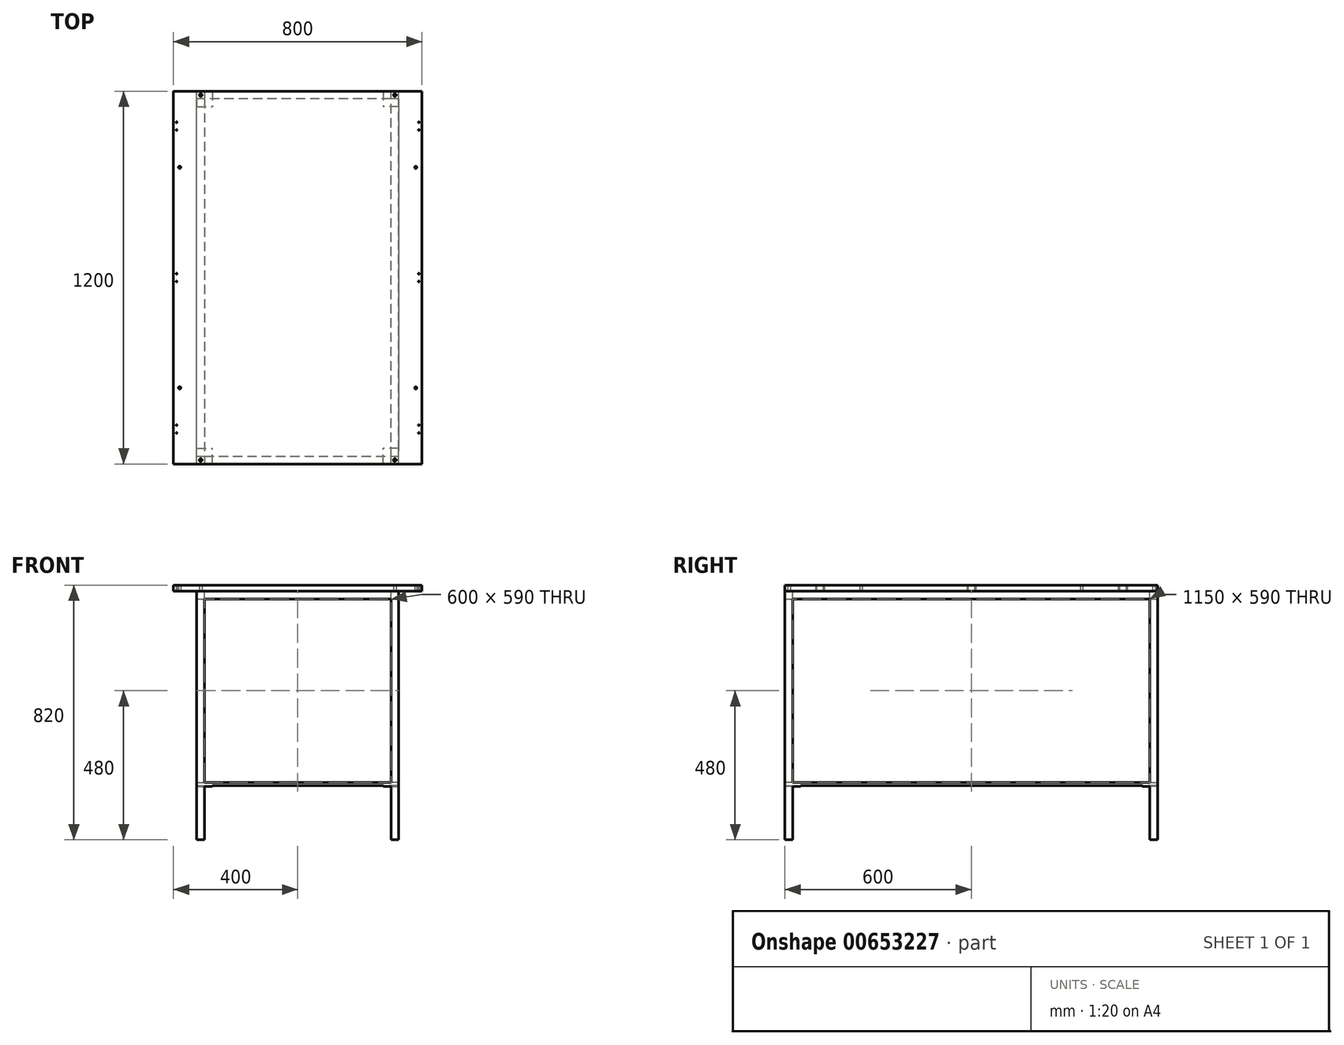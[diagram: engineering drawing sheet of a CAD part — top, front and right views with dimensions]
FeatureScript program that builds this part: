
annotation { "Feature Type Name" : "Feature", "Feature Type Description" : "" }
export const myFeature = defineFeature(function(context is Context, id is Id, definition is map)
    precondition{}
    {
        {
            var Q0;
            Q0=qCreatedBy(makeId("Top.planeOp"),FACE);
            var sketch = newSketch(context, id + "F0", { "sketchPlane" : qUnion([Q0])});
            skLineSegment(sketch, "E0.bottom", {"start": v(400, 600) * mm, "end": v(-400, 600) * mm});
            skLineSegment(sketch, "E0.top", {"start": v(400, -600) * mm, "end": v(-400, -600) * mm});
            skLineSegment(sketch, "E0.left", {"start": v(400, 600) * mm, "end": v(400, -600) * mm});
            skLineSegment(sketch, "E0.right", {"start": v(-400, 600) * mm, "end": v(-400, -600) * mm});
            skPoint(sketch, "E0.middle", {"position": v(0, 0) * mm});
            skSolve(sketch);
        }
        {
            var Q0;
            Q0=makeQuery(id+"F0.imprint","IMPRINT",FACE,{"disambiguationData":[TD([[makeQuery(id+"F0.imprint","IMPRINT",EDGE,{"derivedFrom":sQuery(id+"F0.wireOp",EDGE,"E0.bottom")}),1.0]])]});
            extrude(context, id + "F1", {"entities" : qUnion([Q0]), "depth" : 20 * mm, "offsetDistance" : 25 * mm});
        }
        {
            var Q0;
            Q0=makeQuery(id+"F1.opExtrude","CAP_FACE",FACE,{"disambiguationData":[OSD([sQuery(id+"F0.wireOp",EDGE,"E0.bottom"),sQuery(id+"F0.wireOp",EDGE,"E0.top"),sQuery(id+"F0.wireOp",EDGE,"E0.left"),sQuery(id+"F0.wireOp",EDGE,"E0.right")])],"isStart":true});
            var sketch = newSketch(context, id + "F2", { "sketchPlane" : qUnion([Q0])});
            skLineSegment(sketch, "E1.bottom", {"start": v(-325, 600) * mm, "end": v(-300, 600) * mm});
            skLineSegment(sketch, "E1.top", {"start": v(-325, 575) * mm, "end": v(-300, 575) * mm});
            skLineSegment(sketch, "E1.left", {"start": v(-325, 600) * mm, "end": v(-325, 575) * mm});
            skLineSegment(sketch, "E1.right", {"start": v(-300, 600) * mm, "end": v(-300, 575) * mm});
            skLineSegment(sketch, "E2.bottom", {"start": v(300, 600) * mm, "end": v(325, 600) * mm});
            skLineSegment(sketch, "E2.top", {"start": v(300, 575) * mm, "end": v(325, 575) * mm});
            skLineSegment(sketch, "E2.left", {"start": v(300, 600) * mm, "end": v(300, 575) * mm});
            skLineSegment(sketch, "E2.right", {"start": v(325, 600) * mm, "end": v(325, 575) * mm});
            skLineSegment(sketch, "E3.bottom", {"start": v(-300, -575) * mm, "end": v(-325, -575) * mm});
            skLineSegment(sketch, "E3.top", {"start": v(-300, -600) * mm, "end": v(-325, -600) * mm});
            skLineSegment(sketch, "E3.left", {"start": v(-300, -575) * mm, "end": v(-300, -600) * mm});
            skLineSegment(sketch, "E3.right", {"start": v(-325, -575) * mm, "end": v(-325, -600) * mm});
            skLineSegment(sketch, "E4.bottom", {"start": v(300, -575) * mm, "end": v(325, -575) * mm});
            skLineSegment(sketch, "E4.top", {"start": v(300, -600) * mm, "end": v(325, -600) * mm});
            skLineSegment(sketch, "E4.left", {"start": v(300, -575) * mm, "end": v(300, -600) * mm});
            skLineSegment(sketch, "E4.right", {"start": v(325, -575) * mm, "end": v(325, -600) * mm});
            skSolve(sketch);
        }
        {
            var Q0;
            Q0 = qSketchRegion(id + "F2", true);
            extrude(context, id + "F3", {"entities" : qUnion([Q0]), "depth" : 800 * mm, "offsetDistance" : 25 * mm});
        }
        {
            var Q0;
            Q0=makeQuery(id+"F1.opExtrude","CAP_FACE",FACE,{"disambiguationData":[OSD([sQuery(id+"F0.wireOp",EDGE,"E0.bottom"),sQuery(id+"F0.wireOp",EDGE,"E0.top"),sQuery(id+"F0.wireOp",EDGE,"E0.left"),sQuery(id+"F0.wireOp",EDGE,"E0.right")])],"isStart":true});
            var sketch = newSketch(context, id + "F4", { "sketchPlane" : qUnion([Q0])});
            skLineSegment(sketch, "E5.0", {"start": v(-300, 600) * mm, "end": v(-300, 575) * mm});
            skLineSegment(sketch, "E6.0", {"start": v(-325, 575) * mm, "end": v(-300, 575) * mm});
            skLineSegment(sketch, "E7.0", {"start": v(-300, -575) * mm, "end": v(-325, -575) * mm});
            skLineSegment(sketch, "E8.0", {"start": v(-300, -575) * mm, "end": v(-300, -600) * mm});
            skLineSegment(sketch, "E9.0", {"start": v(300, -575) * mm, "end": v(300, -600) * mm});
            skLineSegment(sketch, "E10.0", {"start": v(300, -575) * mm, "end": v(325, -575) * mm});
            skLineSegment(sketch, "E11.0", {"start": v(300, 575) * mm, "end": v(325, 575) * mm});
            skLineSegment(sketch, "E12.0", {"start": v(300, 600) * mm, "end": v(300, 575) * mm});
            skLineSegment(sketch, "E13", {"start": v(-300, 600) * mm, "end": v(300, 600) * mm});
            skLineSegment(sketch, "E14", {"start": v(-300, 575) * mm, "end": v(300, 575) * mm});
            skLineSegment(sketch, "E15", {"start": v(300, 575) * mm, "end": v(300, -575) * mm});
            skLineSegment(sketch, "E16", {"start": v(325, -575) * mm, "end": v(325, 575) * mm});
            skLineSegment(sketch, "E17", {"start": v(300, -575) * mm, "end": v(-300, -575) * mm});
            skLineSegment(sketch, "E18", {"start": v(-300, -600) * mm, "end": v(300, -600) * mm});
            skLineSegment(sketch, "E19", {"start": v(-300, -575) * mm, "end": v(-300, 575) * mm});
            skLineSegment(sketch, "E20", {"start": v(-325, -575) * mm, "end": v(-325, 575) * mm});
            skSolve(sketch);
        }
        {
            var Q0;
            Q0=makeQuery(id+"F4.imprint","IMPRINT",FACE,{"disambiguationData":[TD([[makeQuery(id+"F4.imprint","IMPRINT",EDGE,{"derivedFrom":sQuery(id+"F4.wireOp",EDGE,"E8.0")}),1.0]])]});
            var Q1;
            Q1=makeQuery(id+"F4.imprint","IMPRINT",FACE,{"disambiguationData":[TD([[makeQuery(id+"F4.imprint","IMPRINT",EDGE,{"derivedFrom":sQuery(id+"F4.wireOp",EDGE,"E6.0")}),-1.0]])]});
            var Q2;
            Q2=makeQuery(id+"F4.imprint","IMPRINT",FACE,{"disambiguationData":[TD([[makeQuery(id+"F4.imprint","IMPRINT",EDGE,{"derivedFrom":sQuery(id+"F4.wireOp",EDGE,"E10.0")}),1.0]])]});
            var Q3;
            Q3=makeQuery(id+"F4.imprint","IMPRINT",FACE,{"disambiguationData":[TD([[makeQuery(id+"F4.imprint","IMPRINT",EDGE,{"derivedFrom":sQuery(id+"F4.wireOp",EDGE,"E5.0")}),1.0]])]});
            extrude(context, id + "F5", {"entities" : qUnion([Q0, Q1, Q2, Q3]), "depth" : 25 * mm, "offsetDistance" : 25 * mm});
        }
        {
            var Q0;
            {var subQ0=sQuery(id+"F0.wireOp",EDGE,"E0.left");var subQ1=sQuery(id+"F0.wireOp",EDGE,"E0.bottom");var subQ2=sQuery(id+"F0.wireOp",EDGE,"E0.right");var subQ3=sQuery(id+"F0.wireOp",EDGE,"E0.top");Q0=makeQuery(id+"F5.boolean.opBoolean","SPLIT",FACE,{"disambiguationData":[TD([makeQuery(id+"F1.opExtrude","SWEPT_FACE",FACE,{"disambiguationData":[OSD([subQ1])]})])],"derivedFrom":makeQuery(id+"F1.opExtrude","CAP_FACE",FACE,{"disambiguationData":[OSD([subQ1,subQ3,subQ0,subQ2])],"isStart":true})});}
            var sketch = newSketch(context, id + "F6", { "sketchPlane" : qUnion([Q0])});
            skLineSegment(sketch, "E21", {"start": v(390, 600) * mm, "end": v(390, -600) * mm, "construction": true});
            skPoint(sketch, "E22", {"position": v(390, 500) * mm});
            skPoint(sketch, "E23", {"position": v(390, 475) * mm});
            skPoint(sketch, "E24", {"position": v(390, 12.5) * mm});
            skPoint(sketch, "E25", {"position": v(390, -12.5) * mm});
            skPoint(sketch, "E26", {"position": v(390, -475) * mm});
            skPoint(sketch, "E27", {"position": v(390, -500) * mm});
            skPoint(sketch, "E28.MirrorP", {"position": v(-390, -500) * mm});
            skPoint(sketch, "E29.MirrorP", {"position": v(-390, -475) * mm});
            skPoint(sketch, "E30.MirrorP", {"position": v(-390, -12.5) * mm});
            skPoint(sketch, "E31.MirrorP", {"position": v(-390, 12.5) * mm});
            skPoint(sketch, "E32.MirrorP", {"position": v(-390, 475) * mm});
            skPoint(sketch, "E33.MirrorP", {"position": v(-390, 500) * mm});
            skLineSegment(sketch, "E34.MirrorCS", {"start": v(-390, 600) * mm, "end": v(-390, -600) * mm, "construction": true});
            skPoint(sketch, "E35", {"position": v(380, 355) * mm});
            skPoint(sketch, "E36", {"position": v(380, -355) * mm});
            skPoint(sketch, "E37.MirrorP", {"position": v(-380, 355) * mm});
            skPoint(sketch, "E38.MirrorP", {"position": v(-380, -355) * mm});
            skLineSegment(sketch, "E39.0.0", {"start": v(-325, 600) * mm, "end": v(-325, 575) * mm, "construction": true});
            skLineSegment(sketch, "E39.0.1", {"start": v(-325, 575) * mm, "end": v(-300, 575) * mm, "construction": true});
            skLineSegment(sketch, "E39.0.2", {"start": v(-300, 575) * mm, "end": v(-300, 600) * mm, "construction": true});
            skLineSegment(sketch, "E39.0.3", {"start": v(-300, 600) * mm, "end": v(-325, 600) * mm, "construction": true});
            skLineSegment(sketch, "E40.0.0", {"start": v(300, 600) * mm, "end": v(300, 575) * mm, "construction": true});
            skLineSegment(sketch, "E40.0.1", {"start": v(300, 575) * mm, "end": v(325, 575) * mm, "construction": true});
            skLineSegment(sketch, "E40.0.2", {"start": v(325, 575) * mm, "end": v(325, 600) * mm, "construction": true});
            skLineSegment(sketch, "E40.0.3", {"start": v(325, 600) * mm, "end": v(300, 600) * mm, "construction": true});
            skLineSegment(sketch, "E41.0.0", {"start": v(-325, -600) * mm, "end": v(-300, -600) * mm, "construction": true});
            skLineSegment(sketch, "E41.0.1", {"start": v(-300, -600) * mm, "end": v(-300, -575) * mm, "construction": true});
            skLineSegment(sketch, "E41.0.2", {"start": v(-300, -575) * mm, "end": v(-325, -575) * mm, "construction": true});
            skLineSegment(sketch, "E41.0.3", {"start": v(-325, -575) * mm, "end": v(-325, -600) * mm, "construction": true});
            skLineSegment(sketch, "E42.0.0", {"start": v(300, -575) * mm, "end": v(300, -600) * mm, "construction": true});
            skLineSegment(sketch, "E42.0.1", {"start": v(300, -600) * mm, "end": v(325, -600) * mm, "construction": true});
            skLineSegment(sketch, "E42.0.2", {"start": v(325, -600) * mm, "end": v(325, -575) * mm, "construction": true});
            skLineSegment(sketch, "E42.0.3", {"start": v(325, -575) * mm, "end": v(300, -575) * mm, "construction": true});
            skPoint(sketch, "E43", {"position": v(-312.5, -587.5) * mm});
            skPoint(sketch, "E43.positionSnap0", {"position": v(-325, -587.5) * mm});
            skPoint(sketch, "E43.positionSnap1", {"position": v(-312.5, -575) * mm});
            skPoint(sketch, "E44", {"position": v(-312.5, 587.5) * mm});
            skPoint(sketch, "E44.positionSnap0", {"position": v(-325, 587.5) * mm});
            skPoint(sketch, "E44.positionSnap1", {"position": v(-312.5, 600) * mm});
            skPoint(sketch, "E45", {"position": v(312.5, 587.5) * mm});
            skPoint(sketch, "E45.positionSnap0", {"position": v(300, 587.5) * mm});
            skPoint(sketch, "E45.positionSnap1", {"position": v(312.5, 600) * mm});
            skPoint(sketch, "E46", {"position": v(312.5, -587.5) * mm});
            skPoint(sketch, "E46.positionSnap0", {"position": v(300, -587.5) * mm});
            skPoint(sketch, "E46.positionSnap1", {"position": v(312.5, -575) * mm});
            skSolve(sketch);
        }
        {
            var Q0;
            Q0=sQuery(id+"F6.wireOp",VERTEX,"E22");
            var Q1;
            Q1=sQuery(id+"F6.wireOp",VERTEX,"E23");
            var Q2;
            Q2=sQuery(id+"F6.wireOp",VERTEX,"E24");
            var Q3;
            Q3=sQuery(id+"F6.wireOp",VERTEX,"E25");
            var Q4;
            Q4=sQuery(id+"F6.wireOp",VERTEX,"E27");
            var Q5;
            Q5=sQuery(id+"F6.wireOp",VERTEX,"E26");
            var Q6;
            Q6=sQuery(id+"F6.wireOp",VERTEX,"E28.MirrorP");
            var Q7;
            Q7=sQuery(id+"F6.wireOp",VERTEX,"E29.MirrorP");
            var Q8;
            Q8=sQuery(id+"F6.wireOp",VERTEX,"E30.MirrorP");
            var Q9;
            Q9=sQuery(id+"F6.wireOp",VERTEX,"E31.MirrorP");
            var Q10;
            Q10=sQuery(id+"F6.wireOp",VERTEX,"E32.MirrorP");
            var Q11;
            Q11=sQuery(id+"F6.wireOp",VERTEX,"E33.MirrorP");
            var Q12;
            Q12=makeQuery(id+"F1.opExtrude","SWEPT_BODY",BODY,{"disambiguationData":[OSD([sQuery(id+"F0.wireOp",EDGE,"E0.bottom"),sQuery(id+"F0.wireOp",EDGE,"E0.top"),sQuery(id+"F0.wireOp",EDGE,"E0.left"),sQuery(id+"F0.wireOp",EDGE,"E0.right")])]});
            hole(context, id + "F7", {"style" : HoleStyle.SIMPLE, "endStyle" : HoleEndStyle.THROUGH, "standardTappedOrClearance" : lookupTablePath({ "standard" : "ISO", "engagement" : "75%", "pitch" : "0.7 mm", "size" : "M4", "type" : "Tapped" }), "standardBlindInLast" : lookupTablePath({ "standard" : "ISO", "engagement" : "75%", "pitch" : "0.7 mm", "size" : "M4", "type" : "Tapped" }), "holeDiameter" : 3.3 * mm, "majorDiameter" : 4 * mm, "showTappedDepth" : true, "isTappedThrough" : true, "tappedDepth" : 12 * mm, "tapClearance" : 3, "startFromSketch" : true, "locations" : qUnion([Q0, Q1, Q2, Q3, Q4, Q5, Q6, Q7, Q8, Q9, Q10, Q11]), "scope" : qUnion([Q12])});
        }
        {
            var Q0;
            Q0=makeQuery(id+"F3.opExtrude","SWEPT_BODY",BODY,{"disambiguationData":[OSD([sQuery(id+"F2.wireOp",EDGE,"E1.bottom"),sQuery(id+"F2.wireOp",EDGE,"E1.top"),sQuery(id+"F2.wireOp",EDGE,"E1.left"),sQuery(id+"F2.wireOp",EDGE,"E1.right")])]});
            var Q1;
            Q1=makeQuery(id+"F3.opExtrude","SWEPT_BODY",BODY,{"disambiguationData":[OSD([sQuery(id+"F2.wireOp",EDGE,"E2.bottom"),sQuery(id+"F2.wireOp",EDGE,"E2.top"),sQuery(id+"F2.wireOp",EDGE,"E2.left"),sQuery(id+"F2.wireOp",EDGE,"E2.right")])]});
            var Q2;
            Q2=makeQuery(id+"F3.opExtrude","SWEPT_BODY",BODY,{"disambiguationData":[OSD([sQuery(id+"F2.wireOp",EDGE,"E3.bottom"),sQuery(id+"F2.wireOp",EDGE,"E3.top"),sQuery(id+"F2.wireOp",EDGE,"E3.left"),sQuery(id+"F2.wireOp",EDGE,"E3.right")])]});
            var Q3;
            Q3=makeQuery(id+"F3.opExtrude","SWEPT_BODY",BODY,{"disambiguationData":[OSD([sQuery(id+"F2.wireOp",EDGE,"E4.bottom"),sQuery(id+"F2.wireOp",EDGE,"E4.top"),sQuery(id+"F2.wireOp",EDGE,"E4.left"),sQuery(id+"F2.wireOp",EDGE,"E4.right")])]});
            var Q4;
            Q4=makeQuery(id+"F5.opExtrude","SWEPT_BODY",BODY,{"disambiguationData":[OSD([sQuery(id+"F4.wireOp",EDGE,"E5.0"),sQuery(id+"F4.wireOp",EDGE,"E12.0"),sQuery(id+"F4.wireOp",EDGE,"E13"),sQuery(id+"F4.wireOp",EDGE,"E14")])]});
            var Q5;
            Q5=makeQuery(id+"F5.opExtrude","SWEPT_BODY",BODY,{"disambiguationData":[OSD([sQuery(id+"F4.wireOp",EDGE,"E6.0"),sQuery(id+"F4.wireOp",EDGE,"E7.0"),sQuery(id+"F4.wireOp",EDGE,"E19"),sQuery(id+"F4.wireOp",EDGE,"E20")])]});
            var Q6;
            Q6=makeQuery(id+"F5.opExtrude","SWEPT_BODY",BODY,{"disambiguationData":[OSD([sQuery(id+"F4.wireOp",EDGE,"E8.0"),sQuery(id+"F4.wireOp",EDGE,"E9.0"),sQuery(id+"F4.wireOp",EDGE,"E17"),sQuery(id+"F4.wireOp",EDGE,"E18")])]});
            var Q7;
            Q7=makeQuery(id+"F5.opExtrude","SWEPT_BODY",BODY,{"disambiguationData":[OSD([sQuery(id+"F4.wireOp",EDGE,"E10.0"),sQuery(id+"F4.wireOp",EDGE,"E11.0"),sQuery(id+"F4.wireOp",EDGE,"E15"),sQuery(id+"F4.wireOp",EDGE,"E16")])]});
            booleanBodies(context, id + "F8", {"operationType" : BooleanOperationType.UNION, "tools" : qUnion([Q0, Q1, Q2, Q3, Q4, Q5, Q6, Q7])});
        }
        {
            var Q0;
            Q0=sQuery(id+"F6.wireOp",VERTEX,"E35");
            var Q1;
            Q1=sQuery(id+"F6.wireOp",VERTEX,"E36");
            var Q2;
            Q2=sQuery(id+"F6.wireOp",VERTEX,"E38.MirrorP");
            var Q3;
            Q3=sQuery(id+"F6.wireOp",VERTEX,"E37.MirrorP");
            var Q4;
            Q4=makeQuery(id+"F1.opExtrude","SWEPT_BODY",BODY,{"disambiguationData":[OSD([sQuery(id+"F0.wireOp",EDGE,"E0.bottom"),sQuery(id+"F0.wireOp",EDGE,"E0.top"),sQuery(id+"F0.wireOp",EDGE,"E0.left"),sQuery(id+"F0.wireOp",EDGE,"E0.right")])]});
            hole(context, id + "F9", {"style" : HoleStyle.SIMPLE, "endStyle" : HoleEndStyle.THROUGH, "holeDiameter" : 7.5 * mm, "majorDiameter" : 5 * mm, "isTappedThrough" : true, "tappedDepth" : 12 * mm, "tapClearance" : 3, "startFromSketch" : true, "locations" : qUnion([Q0, Q1, Q2, Q3]), "scope" : qUnion([Q4])});
        }
        {
            var Q0;
            Q0=sQuery(id+"F6.wireOp",VERTEX,"E44");
            var Q1;
            Q1=sQuery(id+"F6.wireOp",VERTEX,"E45");
            var Q2;
            Q2=sQuery(id+"F6.wireOp",VERTEX,"E46");
            var Q3;
            Q3=sQuery(id+"F6.wireOp",VERTEX,"E43");
            var Q4;
            Q4=makeQuery(id+"F1.opExtrude","SWEPT_BODY",BODY,{"disambiguationData":[OSD([sQuery(id+"F0.wireOp",EDGE,"E0.bottom"),sQuery(id+"F0.wireOp",EDGE,"E0.top"),sQuery(id+"F0.wireOp",EDGE,"E0.left"),sQuery(id+"F0.wireOp",EDGE,"E0.right")])]});
            hole(context, id + "F10", {"style" : HoleStyle.SIMPLE, "endStyle" : HoleEndStyle.THROUGH, "standardTappedOrClearance" : lookupTablePath({ "standard" : "ISO", "fit" : "Normal", "size" : "M8", "type" : "Clearance" }), "standardBlindInLast" : lookupTablePath({ "fit" : "Standard", "standard" : "ISO", "size" : "M8", "type" : "Clearance" }), "holeDiameter" : 8.8 * mm, "majorDiameter" : 5 * mm, "isTappedThrough" : true, "tappedDepth" : 12 * mm, "tapClearance" : 3, "startFromSketch" : true, "locations" : qUnion([Q0, Q1, Q2, Q3]), "scope" : qUnion([Q4])});
        }
        {
            var Q0;
            Q0=makeQuery(id+"F5.opExtrude","CAP_FACE",FACE,{"disambiguationData":[OSD([sQuery(id+"F4.wireOp",EDGE,"E5.0"),sQuery(id+"F4.wireOp",EDGE,"E12.0"),sQuery(id+"F4.wireOp",EDGE,"E13"),sQuery(id+"F4.wireOp",EDGE,"E14")])],"isStart":false});
            cPlane(context, id + "F11", {"entities" : qUnion([Q0]), "cplaneType" : CPlaneType.OFFSET, "offset" : 300 * mm, "width" : 150 * mm, "height" : 150 * mm});
        }
        {
            var Q0;
            Q0=qCreatedBy(id+"F11.planeOp",FACE);
            cPlane(context, id + "F12", {"entities" : qUnion([Q0]), "cplaneType" : CPlaneType.OFFSET, "offset" : 300 * mm, "width" : 150 * mm, "height" : 150 * mm});
        }
        {
            var Q0;
            Q0=qCreatedBy(id+"F12.planeOp",FACE);
            var sketch = newSketch(context, id + "F13", { "sketchPlane" : qUnion([Q0])});
            skLineSegment(sketch, "E47.0.1", {"start": v(300, 575) * mm, "end": v(325, 575) * mm});
            skLineSegment(sketch, "E47.0.3", {"start": v(325, 575) * mm, "end": v(300, 575) * mm});
            skLineSegment(sketch, "E48.0.1", {"start": v(300, 600) * mm, "end": v(300, 575) * mm});
            skLineSegment(sketch, "E48.0.3", {"start": v(300, 575) * mm, "end": v(300, 600) * mm});
            skLineSegment(sketch, "E49.0.1", {"start": v(-300, -575) * mm, "end": v(-325, -575) * mm});
            skLineSegment(sketch, "E49.0.3", {"start": v(-325, -575) * mm, "end": v(-300, -575) * mm});
            skLineSegment(sketch, "E50.0.0", {"start": v(-300, -600) * mm, "end": v(-300, -575) * mm});
            skLineSegment(sketch, "E50.0.2", {"start": v(-300, -575) * mm, "end": v(-300, -600) * mm});
            skLineSegment(sketch, "E51", {"start": v(325, 575) * mm, "end": v(325, 550) * mm});
            skLineSegment(sketch, "E52", {"start": v(325, 550) * mm, "end": v(275, 550) * mm});
            skLineSegment(sketch, "E53", {"start": v(300, 600) * mm, "end": v(275, 600) * mm});
            skLineSegment(sketch, "E54", {"start": v(275, 600) * mm, "end": v(275, 550) * mm});
            skLineSegment(sketch, "E55.MirrorCS", {"start": v(300, -575) * mm, "end": v(300, -600) * mm});
            skLineSegment(sketch, "E56.MirrorCS", {"start": v(325, -575) * mm, "end": v(325, -550) * mm});
            skLineSegment(sketch, "E57.MirrorCS", {"start": v(325, -575) * mm, "end": v(300, -575) * mm});
            skLineSegment(sketch, "E58.MirrorCS", {"start": v(300, -600) * mm, "end": v(300, -575) * mm});
            skLineSegment(sketch, "E59.MirrorCS", {"start": v(325, -550) * mm, "end": v(275, -550) * mm});
            skLineSegment(sketch, "E60.MirrorCS", {"start": v(300, -575) * mm, "end": v(325, -575) * mm});
            skLineSegment(sketch, "E61.MirrorCS", {"start": v(275, -600) * mm, "end": v(275, -550) * mm});
            skLineSegment(sketch, "E62.MirrorCS", {"start": v(300, -600) * mm, "end": v(275, -600) * mm});
            skLineSegment(sketch, "E63.MirrorCS", {"start": v(-300, 575) * mm, "end": v(-300, 600) * mm});
            skLineSegment(sketch, "E64.MirrorCS", {"start": v(-325, 575) * mm, "end": v(-300, 575) * mm});
            skLineSegment(sketch, "E65.MirrorCS", {"start": v(-300, 600) * mm, "end": v(-300, 575) * mm});
            skLineSegment(sketch, "E66.MirrorCS", {"start": v(-300, 575) * mm, "end": v(-325, 575) * mm});
            skLineSegment(sketch, "E67.MirrorCS", {"start": v(-300, -600) * mm, "end": v(-275, -600) * mm});
            skLineSegment(sketch, "E68.MirrorCS", {"start": v(-325, -575) * mm, "end": v(-325, -550) * mm});
            skLineSegment(sketch, "E69.MirrorCS", {"start": v(-325, 550) * mm, "end": v(-275, 550) * mm});
            skLineSegment(sketch, "E70.MirrorCS", {"start": v(-325, -550) * mm, "end": v(-275, -550) * mm});
            skLineSegment(sketch, "E71.MirrorCS", {"start": v(-325, 575) * mm, "end": v(-325, 550) * mm});
            skLineSegment(sketch, "E72.MirrorCS", {"start": v(-275, 600) * mm, "end": v(-275, 550) * mm});
            skLineSegment(sketch, "E73.MirrorCS", {"start": v(-275, -600) * mm, "end": v(-275, -550) * mm});
            skLineSegment(sketch, "E74.MirrorCS", {"start": v(-300, 600) * mm, "end": v(-275, 600) * mm});
            skSolve(sketch);
        }
        {
            var Q0;
            Q0 = qSketchRegion(id + "F13", true);
            extrude(context, id + "F14", {"entities" : qUnion([Q0]), "operationType" : NewBodyOperationType.ADD, "depth" : 2.5 * mm, "offsetDistance" : 25 * mm});
        }
        {
            var Q0;
            Q0=makeQuery(id+"F14.opExtrude","CAP_FACE",FACE,{"disambiguationData":[OSD([sQuery(id+"F13.wireOp",EDGE,"E47.0.3"),sQuery(id+"F13.wireOp",EDGE,"E48.0.3"),sQuery(id+"F13.wireOp",EDGE,"E51"),sQuery(id+"F13.wireOp",EDGE,"E52"),sQuery(id+"F13.wireOp",EDGE,"E53"),sQuery(id+"F13.wireOp",EDGE,"E54")])],"isStart":true});
            var sketch = newSketch(context, id + "F15", { "sketchPlane" : qUnion([Q0])});
            skLineSegment(sketch, "E75.0.0", {"start": v(275, -600) * mm, "end": v(300, -600) * mm});
            skLineSegment(sketch, "E75.0.1", {"start": v(300, -600) * mm, "end": v(300, -575) * mm});
            skLineSegment(sketch, "E75.0.2", {"start": v(300, -575) * mm, "end": v(325, -575) * mm});
            skLineSegment(sketch, "E75.0.3", {"start": v(325, -575) * mm, "end": v(325, -550) * mm});
            skLineSegment(sketch, "E75.0.4", {"start": v(325, -550) * mm, "end": v(275, -550) * mm});
            skLineSegment(sketch, "E75.0.5", {"start": v(275, -550) * mm, "end": v(275, -600) * mm});
            skLineSegment(sketch, "E76.0.0", {"start": v(-275, -600) * mm, "end": v(-275, -550) * mm});
            skLineSegment(sketch, "E76.0.1", {"start": v(-275, -550) * mm, "end": v(-325, -550) * mm});
            skLineSegment(sketch, "E76.0.2", {"start": v(-325, -550) * mm, "end": v(-325, -575) * mm});
            skLineSegment(sketch, "E76.0.3", {"start": v(-325, -575) * mm, "end": v(-300, -575) * mm});
            skLineSegment(sketch, "E76.0.4", {"start": v(-300, -575) * mm, "end": v(-300, -600) * mm});
            skLineSegment(sketch, "E76.0.5", {"start": v(-300, -600) * mm, "end": v(-275, -600) * mm});
            skLineSegment(sketch, "E77.0.0", {"start": v(300, 600) * mm, "end": v(275, 600) * mm});
            skLineSegment(sketch, "E77.0.1", {"start": v(275, 600) * mm, "end": v(275, 550) * mm});
            skLineSegment(sketch, "E77.0.2", {"start": v(275, 550) * mm, "end": v(325, 550) * mm});
            skLineSegment(sketch, "E77.0.3", {"start": v(325, 550) * mm, "end": v(325, 575) * mm});
            skLineSegment(sketch, "E77.0.4", {"start": v(325, 575) * mm, "end": v(300, 575) * mm});
            skLineSegment(sketch, "E77.0.5", {"start": v(300, 575) * mm, "end": v(300, 600) * mm});
            skLineSegment(sketch, "E78.0.0", {"start": v(-275, 600) * mm, "end": v(-300, 600) * mm});
            skLineSegment(sketch, "E78.0.1", {"start": v(-300, 600) * mm, "end": v(-300, 575) * mm});
            skLineSegment(sketch, "E78.0.2", {"start": v(-300, 575) * mm, "end": v(-325, 575) * mm});
            skLineSegment(sketch, "E78.0.3", {"start": v(-325, 575) * mm, "end": v(-325, 550) * mm});
            skLineSegment(sketch, "E78.0.4", {"start": v(-325, 550) * mm, "end": v(-275, 550) * mm});
            skLineSegment(sketch, "E78.0.5", {"start": v(-275, 550) * mm, "end": v(-275, 600) * mm});
            skLineSegment(sketch, "E79", {"start": v(275, -600) * mm, "end": v(-275, -600) * mm});
            skLineSegment(sketch, "E80", {"start": v(-325, -550) * mm, "end": v(-325, 550) * mm});
            skLineSegment(sketch, "E81", {"start": v(275, 600) * mm, "end": v(-275, 600) * mm});
            skLineSegment(sketch, "E82", {"start": v(325, 550) * mm, "end": v(325, -550) * mm});
            skSolve(sketch);
        }
        {
            var Q0;
            Q0=makeQuery(id+"F15.imprint","IMPRINT",FACE,{"disambiguationData":[TD([[makeQuery(id+"F15.imprint","IMPRINT",EDGE,{"derivedFrom":sQuery(id+"F15.wireOp",EDGE,"E75.0.4")}),-1.0]])]});
            var Q1;
            Q1=makeQuery(id+"F15.imprint","IMPRINT",FACE,{"disambiguationData":[TD([[makeQuery(id+"F15.imprint","IMPRINT",EDGE,{"derivedFrom":sQuery(id+"F15.wireOp",EDGE,"E77.0.0")}),1.0]])]});
            var Q2;
            Q2=makeQuery(id+"F15.imprint","IMPRINT",FACE,{"disambiguationData":[TD([[makeQuery(id+"F15.imprint","IMPRINT",EDGE,{"derivedFrom":sQuery(id+"F15.wireOp",EDGE,"E78.0.0")}),1.0]])]});
            var Q3;
            Q3=makeQuery(id+"F15.imprint","IMPRINT",FACE,{"disambiguationData":[TD([[makeQuery(id+"F15.imprint","IMPRINT",EDGE,{"derivedFrom":sQuery(id+"F15.wireOp",EDGE,"E76.0.0")}),1.0]])]});
            var Q4;
            Q4=makeQuery(id+"F15.imprint","IMPRINT",FACE,{"disambiguationData":[TD([[makeQuery(id+"F15.imprint","IMPRINT",EDGE,{"derivedFrom":sQuery(id+"F15.wireOp",EDGE,"E75.0.0")}),-1.0]])]});
            extrude(context, id + "F16", {"entities" : qUnion([Q0, Q1, Q2, Q3, Q4]), "operationType" : NewBodyOperationType.ADD, "depth" : 10 * mm, "offsetDistance" : 25 * mm});
        }
    });
